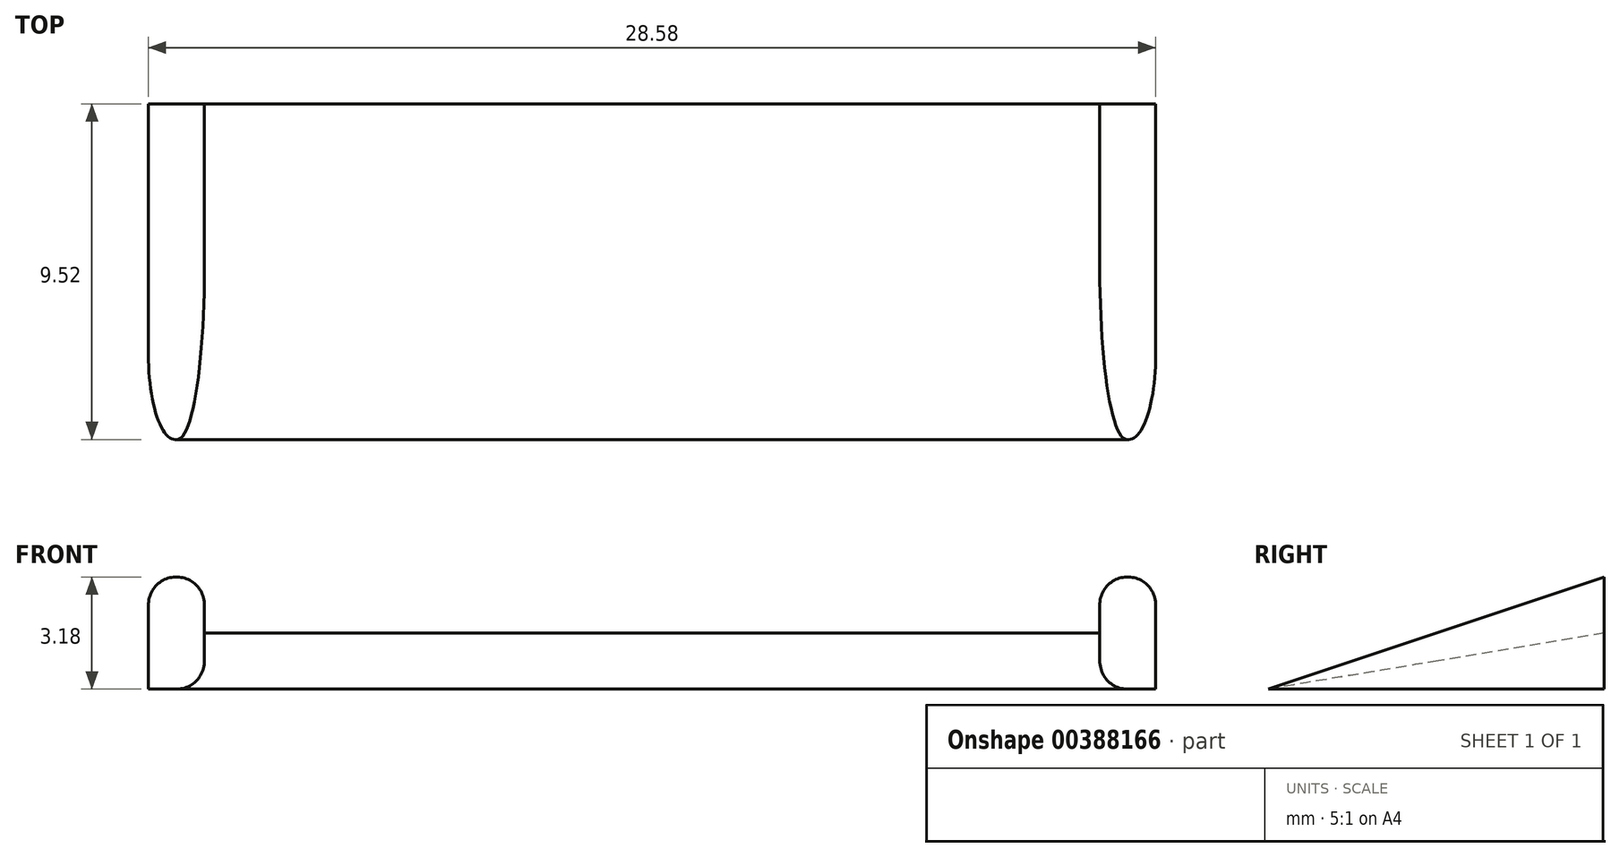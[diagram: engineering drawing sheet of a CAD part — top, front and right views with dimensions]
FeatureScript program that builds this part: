
annotation { "Feature Type Name" : "Feature", "Feature Type Description" : "" }
export const myFeature = defineFeature(function(context is Context, id is Id, definition is map)
    precondition{}
    {
        {
            var Q0;
            Q0=qCreatedBy(makeId("Top.planeOp"),FACE);
            var sketch = newSketch(context, id + "F0", { "sketchPlane" : qUnion([Q0])});
            skLineSegment(sketch, "E0.bottom", {"start": v(-14.29, 4.76) * mm, "end": v(14.29, 4.76) * mm});
            skLineSegment(sketch, "E0.top", {"start": v(-14.29, -4.76) * mm, "end": v(14.29, -4.76) * mm});
            skLineSegment(sketch, "E0.left", {"start": v(-14.29, 4.76) * mm, "end": v(-14.29, -4.76) * mm});
            skLineSegment(sketch, "E0.right", {"start": v(14.29, 4.76) * mm, "end": v(14.29, -4.76) * mm});
            skLineSegment(sketch, "E1", {"start": v(-14.29, 0) * mm, "end": v(14.29, 0) * mm, "construction": true});
            skSolve(sketch);
        }
        {
            var Q0;
            Q0=qSketchRegion(id+"F0",true);
            extrude(context, id + "F1", {"entities" : qUnion([Q0]), "depth" : 1.59 * mm});
        }
        {
            var Q0;
            Q0=makeQuery(id+"F1.opExtrude","SWEPT_FACE",FACE,{"disambiguationData":[OSD([sQuery(id+"F0.wireOp",EDGE,"E0.left")])]});
            var sketch = newSketch(context, id + "F2", { "sketchPlane" : qUnion([Q0])});
            skLineSegment(sketch, "E2", {"start": v(-4.76, 1.59) * mm, "end": v(4.76, 0) * mm});
            skLineSegment(sketch, "E3", {"start": v(4.76, 0) * mm, "end": v(4.76, 1.59) * mm});
            skLineSegment(sketch, "E4", {"start": v(4.76, 1.59) * mm, "end": v(-4.76, 1.59) * mm});
            skSolve(sketch);
        }
        {
            var Q0;
            Q0=qSketchRegion(id+"F2",true);
            var Q1;
            Q1=makeQuery(id+"F1.opExtrude","SWEPT_FACE",FACE,{"disambiguationData":[OSD([sQuery(id+"F0.wireOp",EDGE,"E0.right")])]});
            extrude(context, id + "F3", {"entities" : qUnion([Q0]), "operationType" : NewBodyOperationType.REMOVE, "endBound" : BoundingType.UP_TO_SURFACE, "oppositeDirection" : true, "endBoundEntityFace" : qUnion([Q1]), "depth" : 25.4 * mm});
        }
        {
            var Q0;
            Q0=makeQuery(id+"F1.opExtrude","SWEPT_FACE",FACE,{"disambiguationData":[OSD([sQuery(id+"F0.wireOp",EDGE,"E0.left")])]});
            var sketch = newSketch(context, id + "F4", { "sketchPlane" : qUnion([Q0])});
            skLineSegment(sketch, "E5", {"start": v(-4.76, 0) * mm, "end": v(-4.76, 3.18) * mm});
            skLineSegment(sketch, "E6", {"start": v(-4.76, 3.18) * mm, "end": v(4.76, 0) * mm});
            skLineSegment(sketch, "E7", {"start": v(4.76, 0) * mm, "end": v(-4.76, 0) * mm});
            skSolve(sketch);
        }
        {
            var Q0;
            Q0=qSketchRegion(id+"F4",true);
            extrude(context, id + "F5", {"entities" : qUnion([Q0]), "operationType" : NewBodyOperationType.ADD, "oppositeDirection" : true, "depth" : 1.59 * mm});
        }
        {
            var Q0;
            Q0=makeQuery(id+"F1.opExtrude","SWEPT_FACE",FACE,{"disambiguationData":[OSD([sQuery(id+"F0.wireOp",EDGE,"E0.right")])]});
            var sketch = newSketch(context, id + "F6", { "sketchPlane" : qUnion([Q0])});
            skLineSegment(sketch, "E8", {"start": v(4.76, 0) * mm, "end": v(4.76, 3.18) * mm});
            skLineSegment(sketch, "E9", {"start": v(4.76, 3.18) * mm, "end": v(-4.76, 0) * mm});
            skLineSegment(sketch, "E10", {"start": v(-4.76, 0) * mm, "end": v(4.76, 0) * mm});
            skSolve(sketch);
        }
        {
            var Q0;
            Q0=qSketchRegion(id+"F6",true);
            extrude(context, id + "F7", {"entities" : qUnion([Q0]), "operationType" : NewBodyOperationType.ADD, "oppositeDirection" : true, "depth" : 1.59 * mm});
        }
        {
            var Q0;
            Q0=makeQuery(id+"F5.opExtrude","CAP_EDGE",EDGE,{"disambiguationData":[OSD([sQuery(id+"F4.wireOp",EDGE,"E6")])],"isStart":true});
            var Q1;
            Q1=makeQuery(id+"F5.opExtrude","CAP_EDGE",EDGE,{"disambiguationData":[OSD([sQuery(id+"F4.wireOp",EDGE,"E6")])],"isStart":false});
            var Q2;
            Q2=makeQuery(id+"F7.opExtrude","CAP_EDGE",EDGE,{"disambiguationData":[OSD([sQuery(id+"F6.wireOp",EDGE,"E9")])],"isStart":false});
            var Q3;
            Q3=makeQuery(id+"F7.opExtrude","CAP_EDGE",EDGE,{"disambiguationData":[OSD([sQuery(id+"F6.wireOp",EDGE,"E9")])],"isStart":true});
            fillet(context, id + "F8", {"entities" : qUnion([Q0, Q1, Q2, Q3]), "radius" : 0.76 * mm, "tangentPropagation" : true, "allowEdgeOverflow" : false});
        }
    });
